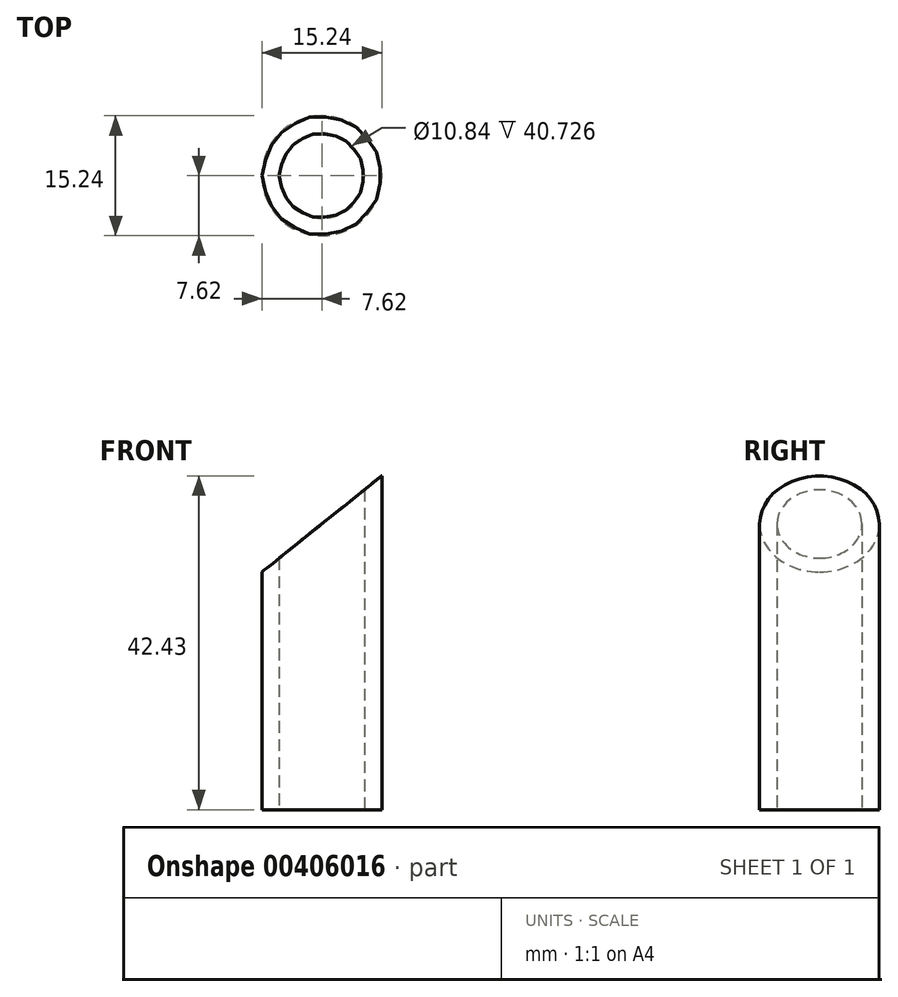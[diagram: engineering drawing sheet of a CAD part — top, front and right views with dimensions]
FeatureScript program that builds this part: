
annotation { "Feature Type Name" : "Feature", "Feature Type Description" : "" }
export const myFeature = defineFeature(function(context is Context, id is Id, definition is map)
    precondition{}
    {
        {
            var Q0;
            Q0=qCreatedBy(makeId("Top.planeOp"),FACE);
            var sketch = newSketch(context, id + "F0", { "sketchPlane" : qUnion([Q0])});
            skCircle(sketch, "E0", {"center": v(0, 0) * mm, "radius": 7.62 * mm});
            skCircle(sketch, "E1", {"center": v(0, 0) * mm, "radius": 5.42 * mm});
            skSolve(sketch);
        }
        {
            var Q0;
            Q0 = qSketchRegion(id + "F0", true);
            extrude(context, id + "F1", {"entities" : qUnion([Q0]), "depth" : 45.72 * mm});
        }
        {
            var Q0;
            Q0=qCreatedBy(makeId("Front.planeOp"),FACE);
            var sketch = newSketch(context, id + "F2", { "sketchPlane" : qUnion([Q0])});
            skLineSegment(sketch, "E2", {"start": v(19.3, 51.8) * mm, "end": v(-24.46, 51.8) * mm});
            skLineSegment(sketch, "E3", {"start": v(-24.46, 51.8) * mm, "end": v(-24.46, 16.68) * mm});
            skLineSegment(sketch, "E4", {"start": v(-24.46, 16.68) * mm, "end": v(19.3, 51.8) * mm});
            skSolve(sketch);
        }
        {
            var Q0;
            Q0 = qSketchRegion(id + "F2", true);
            extrude(context, id + "F3", {"entities" : qUnion([Q0]), "operationType" : NewBodyOperationType.REMOVE, "endBound" : BoundingType.SYMMETRIC, "oppositeDirection" : true, "depth" : 25.4 * mm});
        }
    });
